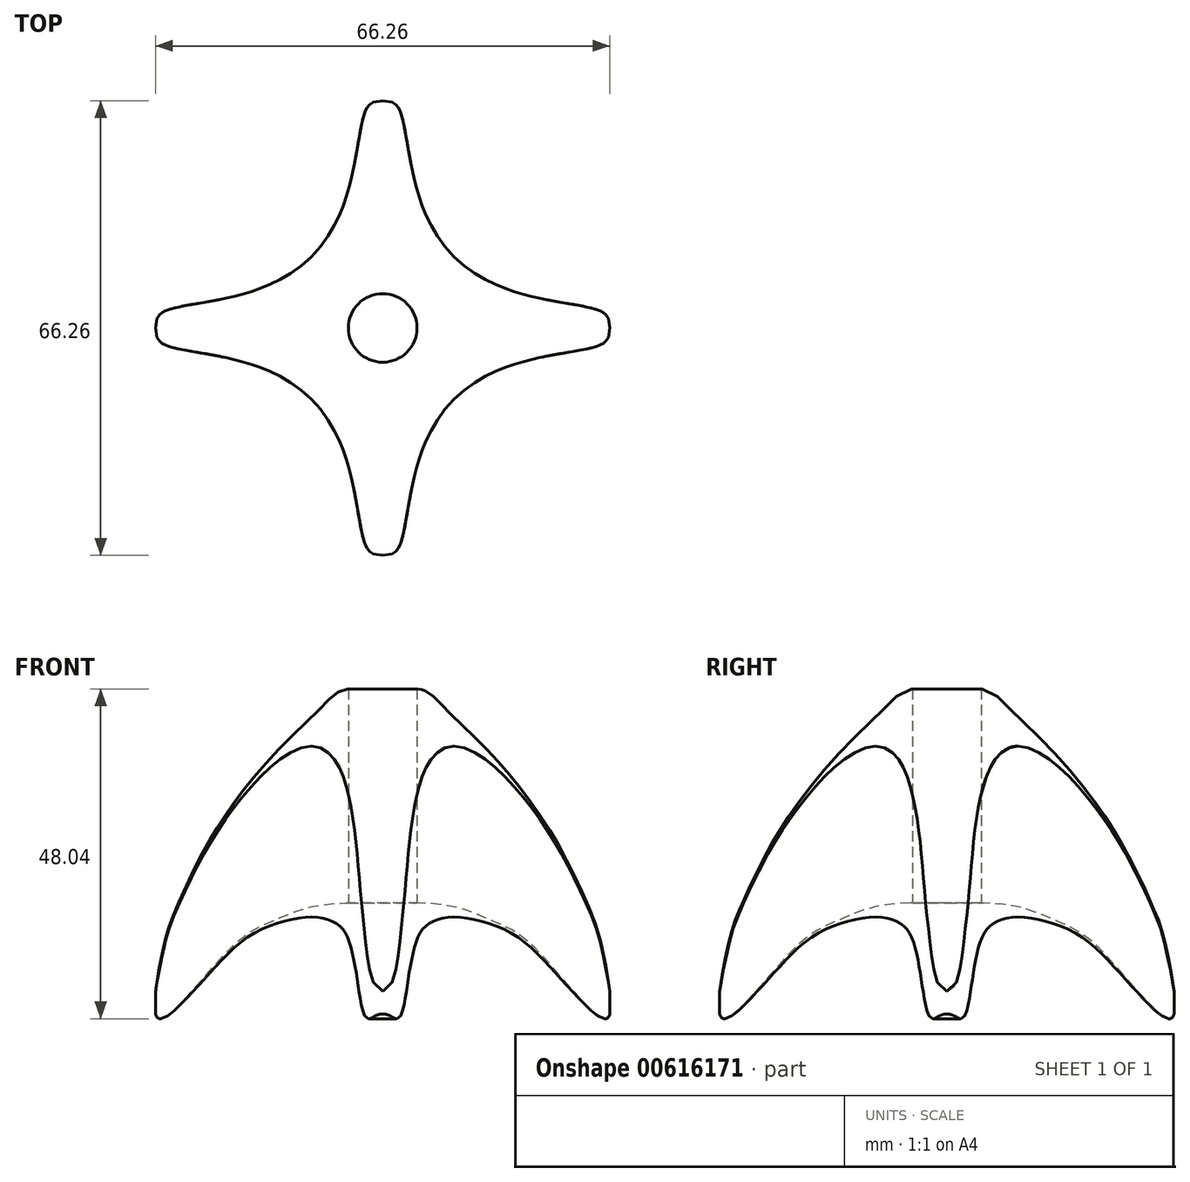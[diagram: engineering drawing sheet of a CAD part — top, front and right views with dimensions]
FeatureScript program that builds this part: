
annotation { "Feature Type Name" : "Feature", "Feature Type Description" : "" }
export const myFeature = defineFeature(function(context is Context, id is Id, definition is map)
    precondition{}
    {
        {
            var Q0;
            Q0=qCreatedBy(makeId("Front.planeOp"),FACE);
            var sketch = newSketch(context, id + "F0", { "sketchPlane" : qUnion([Q0])});
            skLineSegment(sketch, "E0", {"start": v(-5, 0) * mm, "end": v(5, 0) * mm, "construction": true});
            skLineSegment(sketch, "E1", {"start": v(5, 31.2) * mm, "end": v(5, 0) * mm});
            skLineSegment(sketch, "E2", {"start": v(0, 0) * mm, "end": v(0, 15.55) * mm, "construction": true});
            skFitSpline(sketch, "E3", {"points": [v(5, 31.2) * mm, v(8.54, 28.93) * mm, v(16.76, 20.71) * mm, v(22.8, 13) * mm, v(26.52, 6.84) * mm, v(30.76, -2.28) * mm, v(32.17, -7.42) * mm, v(32.69, -16.8) * mm, v(22.03, -6.4) * mm, v(15.6, -2.41) * mm, v(5, 0) * mm], "startDerivative": vector(60.03, 3.2) * mm, "endDerivative": vector(-148.66, -1.47) * mm});
            skSolve(sketch);
        }
        {
            var Q0;
            Q0 = qSketchRegion(id + "F0", true);
            var Q1;
            Q1=sQuery(id+"F0.wireOp",EDGE,"E2");
            revolve(context, id + "F1", {"entities" : qUnion([Q0]), "axis" : qUnion([Q1]), "revolveType" : RevolveType.FULL});
        }
        {
            var Q0;
            Q0=qCreatedBy(makeId("Top.planeOp"),FACE);
            var sketch = newSketch(context, id + "F2", { "sketchPlane" : qUnion([Q0])});
            skLineSegment(sketch, "E4", {"start": v(0, 0) * mm, "end": v(29.85, 29.85) * mm, "construction": true});
            skLineSegment(sketch, "E5", {"start": v(0, 0) * mm, "end": v(33.22, 0) * mm});
            skPoint(sketch, "E6", {"position": v(9.8, 9.8) * mm});
            skLineSegment(sketch, "E7", {"start": v(0, 0) * mm, "end": v(0, 33.13) * mm});
            skLineSegment(sketch, "E8", {"start": v(0, 33.13) * mm, "end": v(-2.27, 33.13) * mm});
            skLineSegment(sketch, "E9", {"start": v(33.22, 0) * mm, "end": v(33.22, -1.26) * mm});
            skFitSpline(sketch, "E10", {"points": [v(0, 33.13) * mm, v(2.25, 32.14) * mm, v(10.38, 10.38) * mm], "startDerivative": vector(9.1, 0) * mm, "endDerivative": vector(28.44, -28.44) * mm});
            skFitSpline(sketch, "E11.MirrorCS", {"points": [v(33.13, 0) * mm, v(32.14, 2.25) * mm, v(10.38, 10.38) * mm], "startDerivative": vector(0, 9.1) * mm, "endDerivative": vector(-28.44, 28.44) * mm});
            skSolve(sketch);
        }
        {
            var Q0;
            Q0 = qSketchRegion(id + "F2", true);
            extrude(context, id + "F3", {"entities" : qUnion([Q0]), "operationType" : NewBodyOperationType.INTERSECT, "depth" : 66.4 * mm, "offsetDistance" : 25 * mm, "symmetric" : true});
        }
        {
            var Q0;
            Q0=makeQuery(id+"F1.opRevolve","SWEPT_BODY",BODY,{"disambiguationData":[OSD([sQuery(id+"F0.wireOp",EDGE,"E1"),sQuery(id+"F0.wireOp",EDGE,"E3")])]});
            var Q1;
            Q1=sQuery(id+"F0.wireOp",EDGE,"E2");
            circularPattern(context, id + "F4", {"operationType" : NewBodyOperationType.ADD, "entities" : qUnion([Q0]), "axis" : qUnion([Q1]), "angle" : 360 * degree, "instanceCount" : 4, "equalSpace" : true});
        }
        {
            var Q0;
            Q0 = qSketchRegion(id + "F2", true);
            extrude(context, id + "F5", {"entities" : qUnion([Q0]), "operationType" : NewBodyOperationType.INTERSECT, "depth" : 73.8 * mm, "offsetDistance" : 25 * mm, "symmetric" : true});
        }
        {
            var Q0;
            Q0=makeQuery(id+"F1.opRevolve","SWEPT_BODY",BODY,{"disambiguationData":[OSD([sQuery(id+"F0.wireOp",EDGE,"E1"),sQuery(id+"F0.wireOp",EDGE,"E3")])]});
            var Q1;
            Q1=sQuery(id+"F0.wireOp",EDGE,"E2");
            circularPattern(context, id + "F6", {"operationType" : NewBodyOperationType.ADD, "entities" : qUnion([Q0]), "axis" : qUnion([Q1]), "angle" : 360 * degree, "instanceCount" : 4, "equalSpace" : true});
        }
    });
